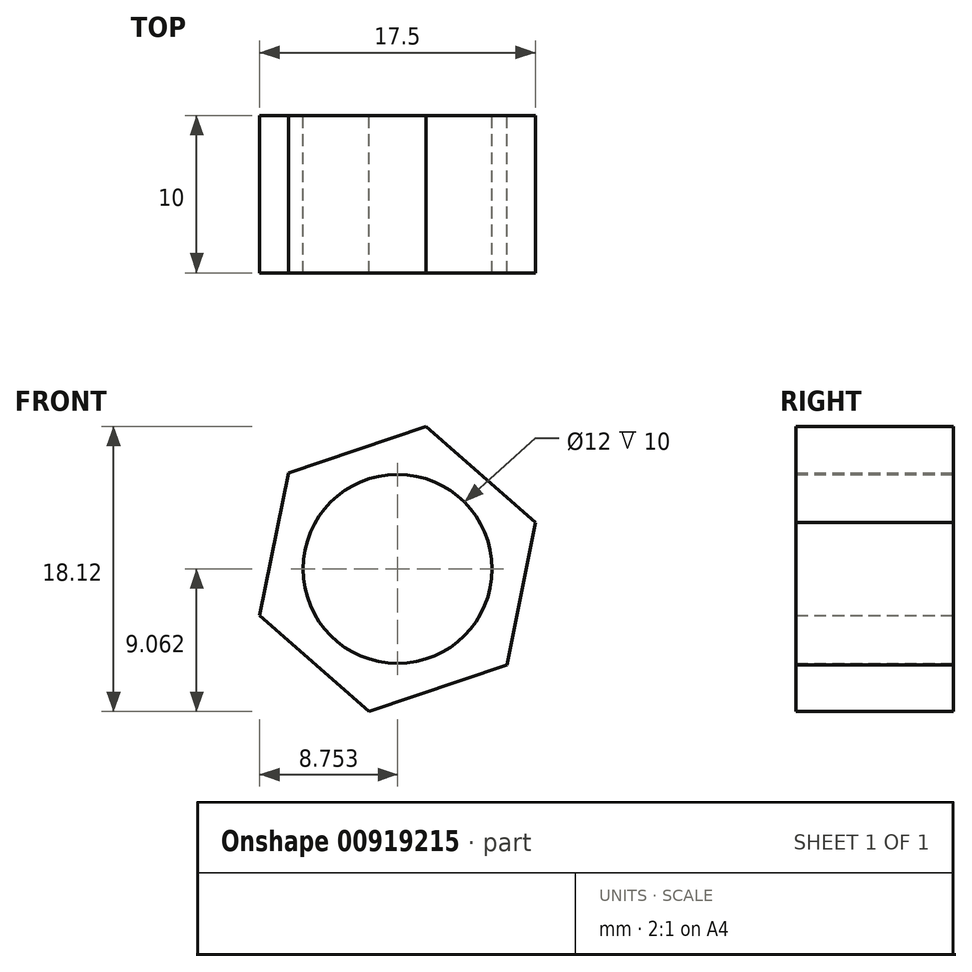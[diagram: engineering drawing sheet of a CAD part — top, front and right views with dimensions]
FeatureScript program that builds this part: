
annotation { "Feature Type Name" : "Feature", "Feature Type Description" : "" }
export const myFeature = defineFeature(function(context is Context, id is Id, definition is map)
    precondition{}
    {
        {
            var Q0;
            Q0=qCreatedBy(makeId("Front.planeOp"),FACE);
            var sketch = newSketch(context, id + "F0", { "sketchPlane" : qUnion([Q0])});
            skCircle(sketch, "E0", {"center": v(-14.99, 3.8) * mm, "radius": 6 * mm});
            skLineSegment(sketch, "E1.0", {"start": v(-8.05, -2.3) * mm, "end": v(-16.8, -5.26) * mm});
            skLineSegment(sketch, "E1.1", {"start": v(-16.8, -5.26) * mm, "end": v(-23.74, 0.85) * mm});
            skLineSegment(sketch, "E1.2", {"start": v(-23.74, 0.85) * mm, "end": v(-21.92, 9.9) * mm});
            skLineSegment(sketch, "E1.3", {"start": v(-21.92, 9.9) * mm, "end": v(-13.17, 12.86) * mm});
            skLineSegment(sketch, "E1.4", {"start": v(-13.17, 12.86) * mm, "end": v(-6.24, 6.76) * mm});
            skLineSegment(sketch, "E1.5", {"start": v(-6.24, 6.76) * mm, "end": v(-8.05, -2.3) * mm});
            skPoint(sketch, "E1.0.midPoint", {"position": v(-12.43, -3.78) * mm});
            skSolve(sketch);
        }
        {
            var Q0;
            Q0=makeQuery(id+"F0.imprint","IMPRINT",FACE,{"disambiguationData":[TD([[makeQuery(id+"F0.imprint","IMPRINT",EDGE,{"derivedFrom":sQuery(id+"F0.wireOp",EDGE,"E0")}),-1.0]])]});
            extrude(context, id + "F1", {"entities" : qUnion([Q0]), "depth" : 10 * mm, "offsetDistance" : 25 * mm});
        }
        {
            var Q0;
            Q0=makeQuery(id+"F1.opExtrude","CAP_FACE",FACE,{"disambiguationData":[OSD([sQuery(id+"F0.wireOp",EDGE,"E0"),sQuery(id+"F0.wireOp",EDGE,"E1.0"),sQuery(id+"F0.wireOp",EDGE,"E1.1"),sQuery(id+"F0.wireOp",EDGE,"E1.2"),sQuery(id+"F0.wireOp",EDGE,"E1.3"),sQuery(id+"F0.wireOp",EDGE,"E1.4"),sQuery(id+"F0.wireOp",EDGE,"E1.5")])],"isStart":false});
            var sketch = newSketch(context, id + "F2", { "sketchPlane" : qUnion([Q0])});
            skCircle(sketch, "E2", {"center": v(-14.99, 3.8) * mm, "radius": 6 * mm});
            skSolve(sketch);
        }
        {
            var Q0;
            Q0=makeQuery(id+"F2.imprint","IMPRINT",FACE,{"disambiguationData":[TD([[makeQuery(id+"F2.imprint","IMPRINT",EDGE,{"derivedFrom":sQuery(id+"F2.wireOp",EDGE,"E2")}),1.0]])]});
            var Q1;
            Q1=sQuery(id+"F2.wireOp",EDGE,"E2");
            extrude(context, id + "F3", {"entities" : qUnion([Q0]), "bodyType" : ToolBodyType.SURFACE, "surfaceEntities" : qUnion([Q1]), "oppositeDirection" : true, "depth" : 25 * mm, "offsetDistance" : 25 * mm});
        }
    });
